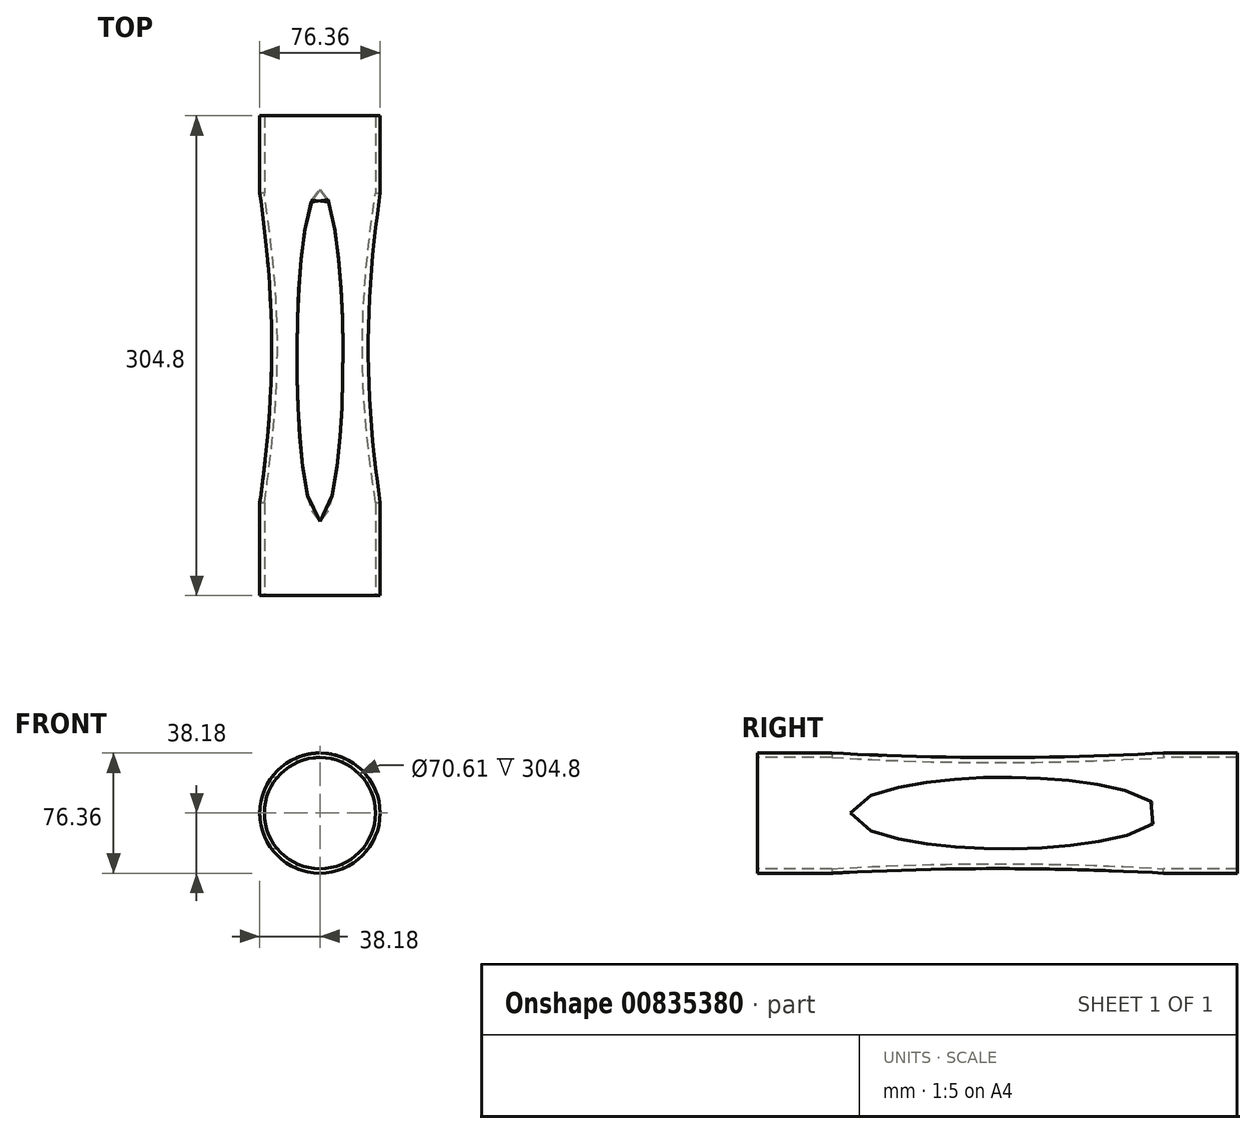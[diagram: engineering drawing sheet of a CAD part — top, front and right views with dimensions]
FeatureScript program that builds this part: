
annotation { "Feature Type Name" : "Feature", "Feature Type Description" : "" }
export const myFeature = defineFeature(function(context is Context, id is Id, definition is map)
    precondition{}
    {
        {
            var Q0;
            Q0=qCreatedBy(makeId("Front.planeOp"),FACE);
            var sketch = newSketch(context, id + "F0", { "sketchPlane" : qUnion([Q0])});
            skCircle(sketch, "E0", {"center": v(0, 0) * mm, "radius": 38.18 * mm});
            skSolve(sketch);
        }
        {
            var Q0;
            Q0=makeQuery(id+"F0.imprint","IMPRINT",FACE,{"disambiguationData":[TD([[makeQuery(id+"F0.imprint","IMPRINT",EDGE,{"derivedFrom":sQuery(id+"F0.wireOp",EDGE,"E0")}),1.0]])]});
            extrude(context, id + "F1", {"entities" : qUnion([Q0]), "depth" : 304.8 * mm, "offsetDistance" : 25.4 * mm});
        }
        {
            var Q0;
            Q0=qCreatedBy(makeId("Top.planeOp"),FACE);
            var sketch = newSketch(context, id + "F2", { "sketchPlane" : qUnion([Q0])});
            skEllipse(sketch, "E1", {"center": v(0, -152.31) * mm, "majorRadius": 105.37 * mm, "minorRadius": 14.67 * mm, "majorAxis": v(0, -1)});
            skSolve(sketch);
        }
        {
            var Q0;
            Q0 = qSketchRegion(id + "F2", true);
            extrude(context, id + "F3", {"entities" : qUnion([Q0]), "operationType" : NewBodyOperationType.REMOVE, "endBound" : BoundingType.SYMMETRIC, "depth" : 177.8 * mm, "offsetDistance" : 25.4 * mm});
        }
        {
            var Q0;
            Q0=makeQuery(id+"F1.opExtrude","CAP_FACE",FACE,{"disambiguationData":[OSD([sQuery(id+"F0.wireOp",EDGE,"E0")])],"isStart":false});
            var sketch = newSketch(context, id + "F4", { "sketchPlane" : qUnion([Q0])});
            skPoint(sketch, "E2", {"position": v(0, 0) * mm});
            skSolve(sketch);
        }
        {
            var Q0;
            Q0=sQuery(id+"F4.wireOp",VERTEX,"E2");
            var Q1;
            Q1=makeQuery(id+"F1.opExtrude","SWEPT_BODY",BODY,{"disambiguationData":[OSD([sQuery(id+"F0.wireOp",EDGE,"E0")])]});
            hole(context, id + "F5", {"style" : HoleStyle.SIMPLE, "endStyle" : HoleEndStyle.BLIND, "holeDiameter" : 70.61 * mm, "majorDiameter" : 6.35 * mm, "holeDepth" : 650 * mm, "isTappedThrough" : true, "tappedDepth" : 12.7 * mm, "tapClearance" : 3, "locations" : qUnion([Q0]), "scope" : qUnion([Q1])});
        }
        {
            var Q0;
            Q0=qCreatedBy(makeId("Right.planeOp"),FACE);
            var sketch = newSketch(context, id + "F6", { "sketchPlane" : qUnion([Q0])});
            skEllipse(sketch, "E3", {"center": v(-147.56, 0) * mm, "majorRadius": 98.27 * mm, "minorRadius": 22.76 * mm, "majorAxis": v(-1, 0)});
            skSolve(sketch);
        }
        {
            var Q0;
            Q0 = qSketchRegion(id + "F6", true);
            extrude(context, id + "F7", {"entities" : qUnion([Q0]), "operationType" : NewBodyOperationType.REMOVE, "endBound" : BoundingType.SYMMETRIC, "oppositeDirection" : true, "depth" : 177.8 * mm, "offsetDistance" : 25.4 * mm});
        }
    });
